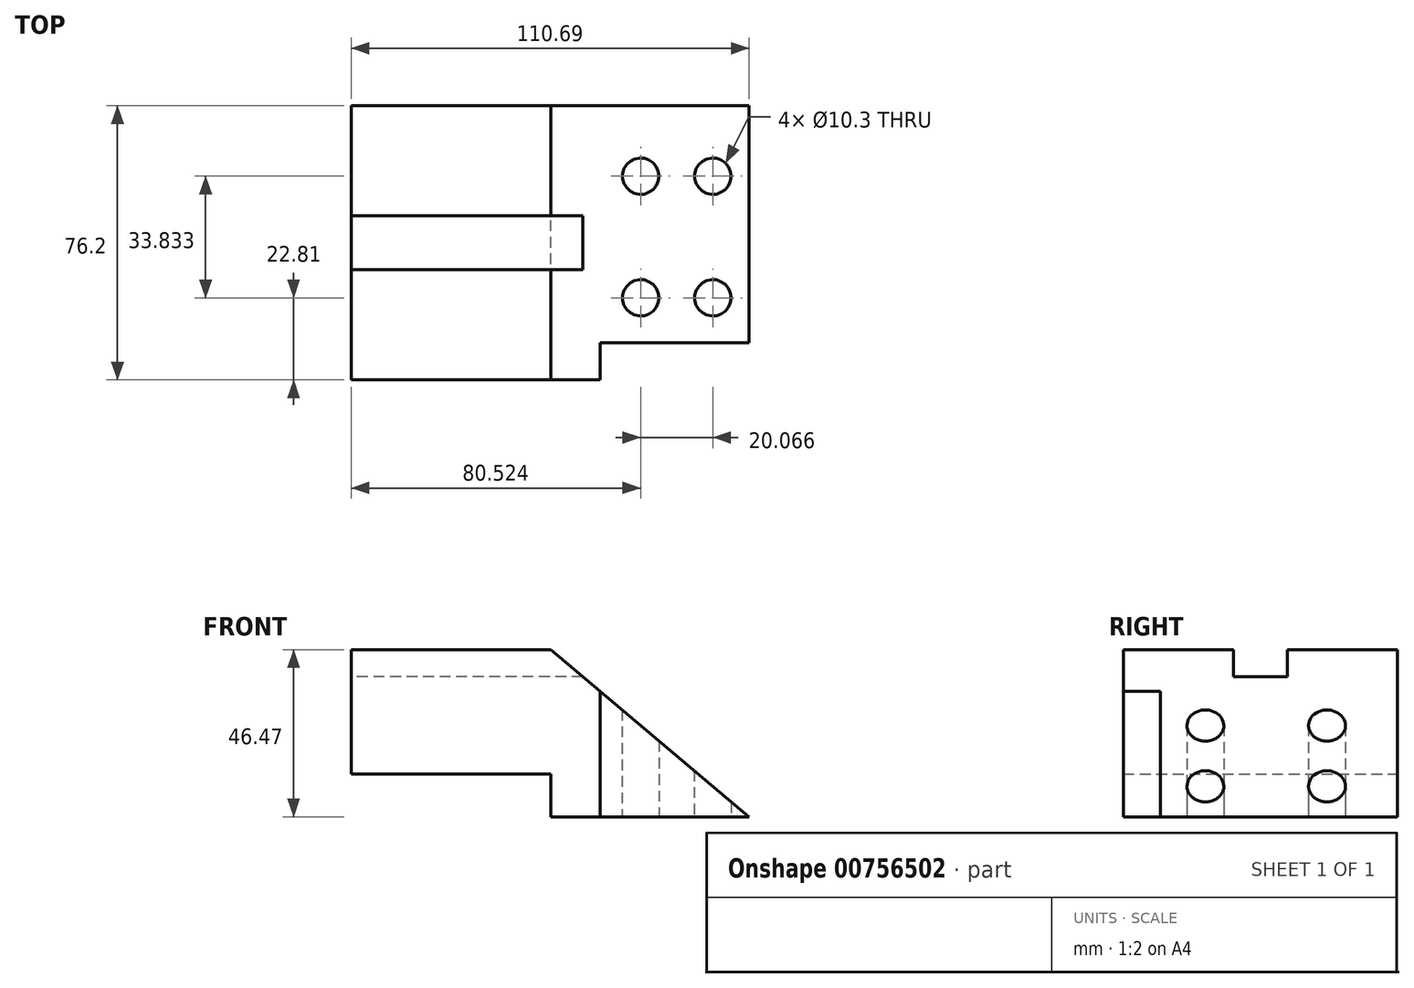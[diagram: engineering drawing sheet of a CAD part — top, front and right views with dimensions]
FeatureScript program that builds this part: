
annotation { "Feature Type Name" : "Feature", "Feature Type Description" : "" }
export const myFeature = defineFeature(function(context is Context, id is Id, definition is map)
    precondition{}
    {
        {
            var Q0;
            Q0=qCreatedBy(makeId("Front.planeOp"),FACE);
            var sketch = newSketch(context, id + "F0", { "sketchPlane" : qUnion([Q0])});
            skLineSegment(sketch, "E0", {"start": v(0, 0) * mm, "end": v(0, 11.88) * mm});
            skLineSegment(sketch, "E1", {"start": v(0, 11.88) * mm, "end": v(-55.5, 11.88) * mm});
            skLineSegment(sketch, "E2", {"start": v(-55.5, 11.88) * mm, "end": v(-55.5, 46.47) * mm});
            skLineSegment(sketch, "E3", {"start": v(-55.5, 46.47) * mm, "end": v(0, 46.47) * mm});
            skLineSegment(sketch, "E4", {"start": v(0, 46.47) * mm, "end": v(55.2, 0) * mm});
            skLineSegment(sketch, "E5", {"start": v(55.2, 0) * mm, "end": v(0, 0) * mm});
            skSolve(sketch);
        }
        {
            var Q0;
            Q0 = qSketchRegion(id + "F0", true);
            extrude(context, id + "F1", {"entities" : qUnion([Q0]), "depth" : 76.2 * mm, "offsetDistance" : 25.4 * mm});
        }
        {
            var Q0;
            Q0=makeQuery(id+"F1.opExtrude","SWEPT_FACE",FACE,{"disambiguationData":[OSD([sQuery(id+"F0.wireOp",EDGE,"E2")])]});
            var sketch = newSketch(context, id + "F2", { "sketchPlane" : qUnion([Q0])});
            skLineSegment(sketch, "E6.bottom", {"start": v(45.57, 46.47) * mm, "end": v(30.63, 46.47) * mm});
            skLineSegment(sketch, "E6.top", {"start": v(45.57, 38.95) * mm, "end": v(30.63, 38.95) * mm});
            skLineSegment(sketch, "E6.left", {"start": v(45.57, 46.47) * mm, "end": v(45.57, 38.95) * mm});
            skLineSegment(sketch, "E6.right", {"start": v(30.63, 46.47) * mm, "end": v(30.63, 38.95) * mm});
            skLineSegment(sketch, "E7", {"start": v(0, 46.47) * mm, "end": v(30.63, 46.47) * mm});
            skLineSegment(sketch, "E8", {"start": v(45.57, 46.47) * mm, "end": v(76.2, 46.47) * mm});
            skSolve(sketch);
        }
        {
            var Q0;
            Q0=makeQuery(id+"F2.imprint","IMPRINT",FACE,{"disambiguationData":[TD([[makeQuery(id+"F2.imprint","IMPRINT",EDGE,{"derivedFrom":sQuery(id+"F2.wireOp",EDGE,"E6.bottom")}),1.0]])]});
            extrude(context, id + "F3", {"entities" : qUnion([Q0]), "operationType" : NewBodyOperationType.REMOVE, "endBound" : BoundingType.THROUGH_ALL, "oppositeDirection" : true, "depth" : 25.4 * mm, "offsetDistance" : 25.4 * mm});
        }
        {
            var Q0;
            Q0=qCreatedBy(makeId("Top.planeOp"),FACE);
            var sketch = newSketch(context, id + "F4", { "sketchPlane" : qUnion([Q0])});
            skLineSegment(sketch, "E9.bottom", {"start": v(55.2, -76.2) * mm, "end": v(13.74, -76.2) * mm});
            skLineSegment(sketch, "E9.top", {"start": v(55.2, -65.87) * mm, "end": v(13.74, -65.87) * mm});
            skLineSegment(sketch, "E9.left", {"start": v(55.2, -76.2) * mm, "end": v(55.2, -65.87) * mm});
            skLineSegment(sketch, "E9.right", {"start": v(13.74, -76.2) * mm, "end": v(13.74, -65.87) * mm});
            skCircle(sketch, "E10", {"center": v(45.1, -53.4) * mm, "radius": 5.15 * mm});
            skCircle(sketch, "E11.0.1.0", {"center": v(45.1, -19.56) * mm, "radius": 5.15 * mm});
            skCircle(sketch, "E11.1.0.0", {"center": v(25.02, -53.4) * mm, "radius": 5.15 * mm});
            skCircle(sketch, "E11.1.1.0", {"center": v(25.02, -19.56) * mm, "radius": 5.15 * mm});
            skLineSegment(sketch, "E11.direction1", {"start": v(45.1, -53.4) * mm, "end": v(25.02, -53.4) * mm, "construction": true});
            skLineSegment(sketch, "E11.direction2", {"start": v(45.1, -53.4) * mm, "end": v(45.1, -19.56) * mm, "construction": true});
            skSolve(sketch);
        }
        {
            var Q0;
            Q0 = qSketchRegion(id + "F4", true);
            var Q1;
            Q1=makeQuery(id+"F1.opExtrude","SWEPT_FACE",FACE,{"disambiguationData":[OSD([sQuery(id+"F0.wireOp",EDGE,"E4")])]});
            extrude(context, id + "F5", {"entities" : qUnion([Q0]), "operationType" : NewBodyOperationType.REMOVE, "endBound" : BoundingType.UP_TO_SURFACE, "depth" : 25.4 * mm, "endBoundEntityFace" : qUnion([Q1]), "offsetDistance" : 25.4 * mm});
        }
    });
